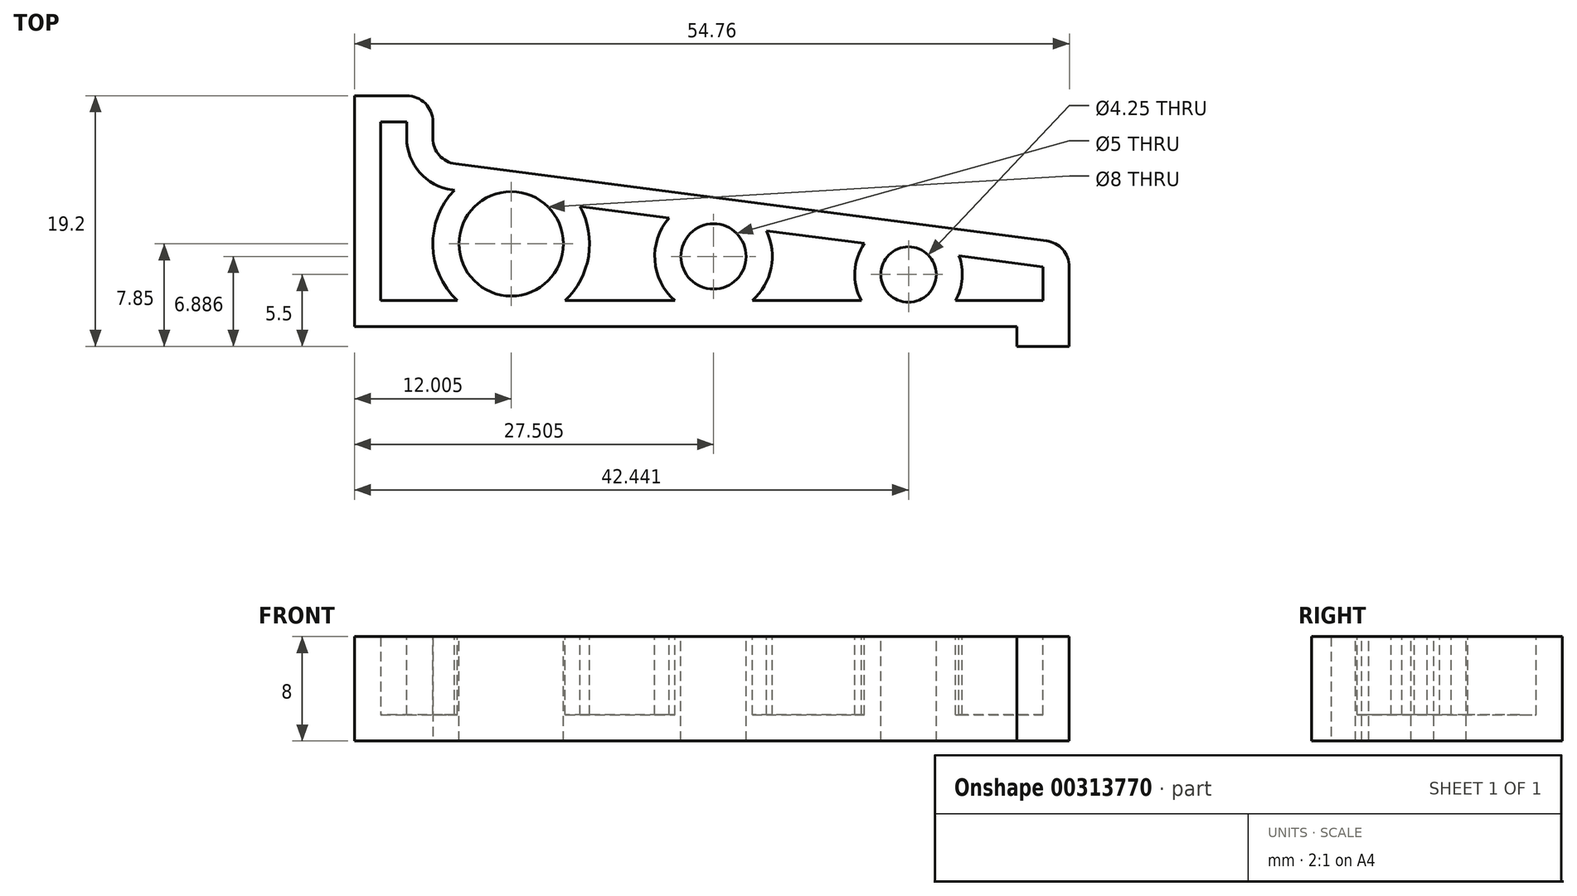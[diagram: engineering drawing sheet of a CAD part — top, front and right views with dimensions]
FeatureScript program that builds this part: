
annotation { "Feature Type Name" : "Feature", "Feature Type Description" : "" }
export const myFeature = defineFeature(function(context is Context, id is Id, definition is map)
    precondition{}
    {
        {
            var Q0;
            Q0=qCreatedBy(makeId("Top.planeOp"),FACE);
            var sketch = newSketch(context, id + "F0", { "sketchPlane" : qUnion([Q0])});
            skLineSegment(sketch, "E0.top", {"start": v(23.38, -6.35) * mm, "end": v(-27.37, -6.35) * mm});
            skLineSegment(sketch, "E0.right", {"start": v(-27.38, 6.35) * mm, "end": v(-27.37, -6.35) * mm});
            skPoint(sketch, "E0.middle", {"position": v(0, 0) * mm});
            skLineSegment(sketch, "E1.right", {"start": v(27.38, 0) * mm, "end": v(27.38, -6.35) * mm});
            skLineSegment(sketch, "E2.top", {"start": v(-27.38, 11.35) * mm, "end": v(-21.38, 11.35) * mm});
            skLineSegment(sketch, "E2.left", {"start": v(-27.38, 6.35) * mm, "end": v(-27.38, 11.35) * mm});
            skLineSegment(sketch, "E2.right", {"start": v(-21.38, 6.35) * mm, "end": v(-21.38, 11.35) * mm});
            skLineSegment(sketch, "E3", {"start": v(-21.38, 6.35) * mm, "end": v(27.38, 0) * mm});
            skPoint(sketch, "E1.bottom.start.orphan", {"position": v(27.38, 6.35) * mm});
            skLineSegment(sketch, "E4.top", {"start": v(27.38, -7.85) * mm, "end": v(23.38, -7.85) * mm});
            skLineSegment(sketch, "E4.left", {"start": v(27.38, -6.35) * mm, "end": v(27.38, -7.85) * mm});
            skLineSegment(sketch, "E4.right", {"start": v(23.38, -6.35) * mm, "end": v(23.38, -7.85) * mm});
            skSolve(sketch);
        }
        {
            var Q0;
            Q0=qSketchRegion(id+"F0",true);
            extrude(context, id + "F1", {"entities" : qUnion([Q0]), "depth" : 8 * mm});
        }
        {
            var Q0;
            Q0=makeQuery(id+"F1.opExtrude","SWEPT_EDGE",EDGE,{"disambiguationData":[OSD([sQuery(id+"F0.wireOp",EDGE,"E2.top"),sQuery(id+"F0.wireOp",EDGE,"E2.right")])]});
            var Q1;
            Q1=makeQuery(id+"F1.opExtrude","SWEPT_EDGE",EDGE,{"disambiguationData":[OSD([sQuery(id+"F0.wireOp",EDGE,"E1.right"),sQuery(id+"F0.wireOp",EDGE,"E3")])]});
            var Q2;
            Q2=makeQuery(id+"F1.opExtrude","SWEPT_EDGE",EDGE,{"disambiguationData":[OSD([sQuery(id+"F0.wireOp",EDGE,"E2.right"),sQuery(id+"F0.wireOp",EDGE,"E3")])]});
            fillet(context, id + "F2", {"entities" : qUnion([Q0, Q1, Q2]), "radius" : 2 * mm, "tangentPropagation" : true, "allowEdgeOverflow" : false});
        }
        {
            var Q0;
            Q0=makeQuery(id+"F1.opExtrude","CAP_FACE",FACE,{"disambiguationData":[OSD([sQuery(id+"F0.wireOp",EDGE,"E0.top"),sQuery(id+"F0.wireOp",EDGE,"E0.right"),sQuery(id+"F0.wireOp",EDGE,"E1.top"),sQuery(id+"F0.wireOp",EDGE,"E1.left"),sQuery(id+"F0.wireOp",EDGE,"E1.right"),sQuery(id+"F0.wireOp",EDGE,"E2.top"),sQuery(id+"F0.wireOp",EDGE,"E2.left"),sQuery(id+"F0.wireOp",EDGE,"E2.right"),sQuery(id+"F0.wireOp",EDGE,"E3")])],"isStart":false});
            var sketch = newSketch(context, id + "F3", { "sketchPlane" : qUnion([Q0])});
            skCircle(sketch, "E5", {"center": v(-15.38, 0) * mm, "radius": 4 * mm});
            skCircle(sketch, "E6", {"center": v(0.12, -0.96) * mm, "radius": 2.5 * mm});
            skCircle(sketch, "E7", {"center": v(15.06, -2.35) * mm, "radius": 2.12 * mm});
            skSolve(sketch);
        }
        {
            var Q0;
            Q0=qSketchRegion(id+"F3",true);
            extrude(context, id + "F4", {"entities" : qUnion([Q0]), "operationType" : NewBodyOperationType.REMOVE, "endBound" : BoundingType.THROUGH_ALL, "oppositeDirection" : true, "depth" : 25 * mm});
        }
        {
            var Q0;
            Q0=makeQuery(id+"F1.opExtrude","CAP_FACE",FACE,{"disambiguationData":[OSD([sQuery(id+"F0.wireOp",EDGE,"E0.top"),sQuery(id+"F0.wireOp",EDGE,"E0.right"),sQuery(id+"F0.wireOp",EDGE,"E1.right"),sQuery(id+"F0.wireOp",EDGE,"E2.top"),sQuery(id+"F0.wireOp",EDGE,"E2.left"),sQuery(id+"F0.wireOp",EDGE,"E2.right"),sQuery(id+"F0.wireOp",EDGE,"E3"),sQuery(id+"F0.wireOp",EDGE,"E4.top"),sQuery(id+"F0.wireOp",EDGE,"E4.left"),sQuery(id+"F0.wireOp",EDGE,"E4.right")])],"isStart":false});
            var Q1;
            Q1=makeQuery(id+"F1.opExtrude","SWEPT_BODY",BODY,{"disambiguationData":[OSD([sQuery(id+"F0.wireOp",EDGE,"E0.top"),sQuery(id+"F0.wireOp",EDGE,"E0.right"),sQuery(id+"F0.wireOp",EDGE,"E1.right"),sQuery(id+"F0.wireOp",EDGE,"E2.top"),sQuery(id+"F0.wireOp",EDGE,"E2.left"),sQuery(id+"F0.wireOp",EDGE,"E2.right"),sQuery(id+"F0.wireOp",EDGE,"E3"),sQuery(id+"F0.wireOp",EDGE,"E4.top"),sQuery(id+"F0.wireOp",EDGE,"E4.left"),sQuery(id+"F0.wireOp",EDGE,"E4.right")])]});
            shell(context, id + "F5", {"entities" : qUnion([Q0]), "parts" : qUnion([Q1]), "thickness" : 2 * mm});
        }
    });
